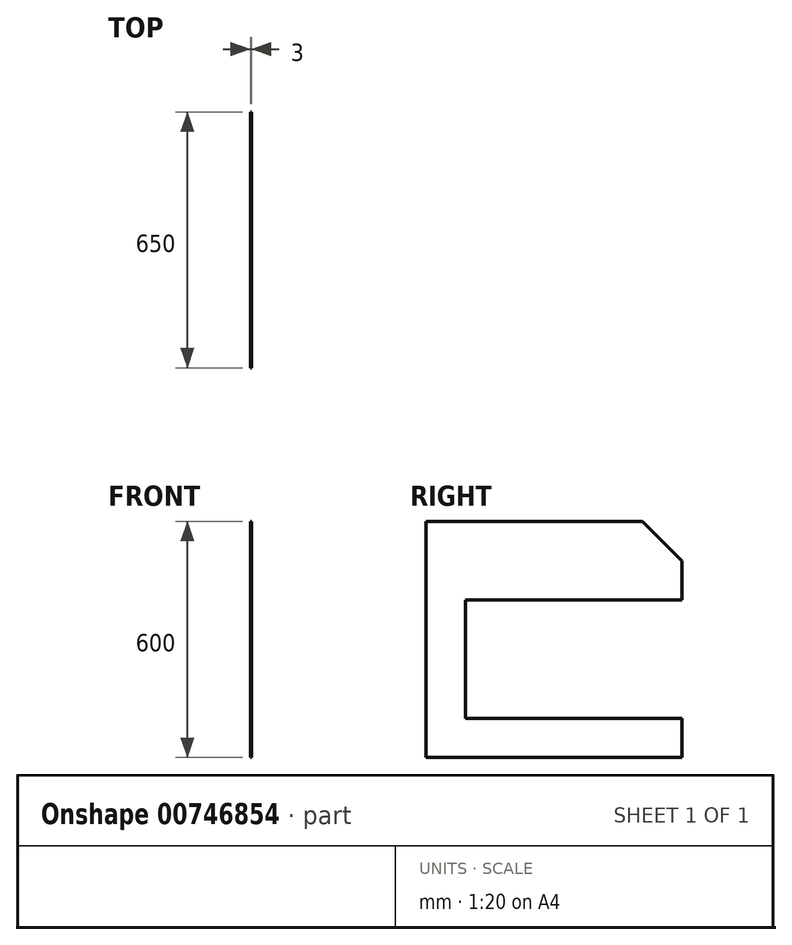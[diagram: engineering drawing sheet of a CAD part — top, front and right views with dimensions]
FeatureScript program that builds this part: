
annotation { "Feature Type Name" : "Feature", "Feature Type Description" : "" }
export const myFeature = defineFeature(function(context is Context, id is Id, definition is map)
    precondition{}
    {
        {
            var Q0;
            Q0=qCreatedBy(makeId("Right.planeOp"),FACE);
            var sketch = newSketch(context, id + "F0", { "sketchPlane" : qUnion([Q0])});
            skLineSegment(sketch, "E0", {"start": v(0, 0) * mm, "end": v(0, 600) * mm});
            skLineSegment(sketch, "E1", {"start": v(0, 600) * mm, "end": v(550, 600) * mm});
            skLineSegment(sketch, "E2", {"start": v(550, 600) * mm, "end": v(650, 500) * mm});
            skLineSegment(sketch, "E3", {"start": v(650, 500) * mm, "end": v(650, 400) * mm});
            skLineSegment(sketch, "E4", {"start": v(650, 400) * mm, "end": v(100, 400) * mm});
            skLineSegment(sketch, "E5", {"start": v(100, 400) * mm, "end": v(100, 100) * mm});
            skLineSegment(sketch, "E6", {"start": v(100, 100) * mm, "end": v(650, 100) * mm});
            skLineSegment(sketch, "E7", {"start": v(650, 100) * mm, "end": v(650, 0) * mm});
            skLineSegment(sketch, "E8", {"start": v(650, 0) * mm, "end": v(0, 0) * mm});
            skLineSegment(sketch, "E9", {"start": v(0, 215.1) * mm, "end": v(100, 215.1) * mm, "construction": true});
            skLineSegment(sketch, "E10", {"start": v(302.3, 400) * mm, "end": v(302.3, 600) * mm, "construction": true});
            skSolve(sketch);
        }
        {
            var Q0;
            Q0=makeQuery(id+"F0.imprint","IMPRINT",FACE,{"disambiguationData":[TD([[makeQuery(id+"F0.imprint","IMPRINT",EDGE,{"derivedFrom":sQuery(id+"F0.wireOp",EDGE,"E0")}),-1.0]])]});
            extrude(context, id + "F1", {"entities" : qUnion([Q0]), "depth" : 3 * mm, "offsetDistance" : 25 * mm});
        }
    });
